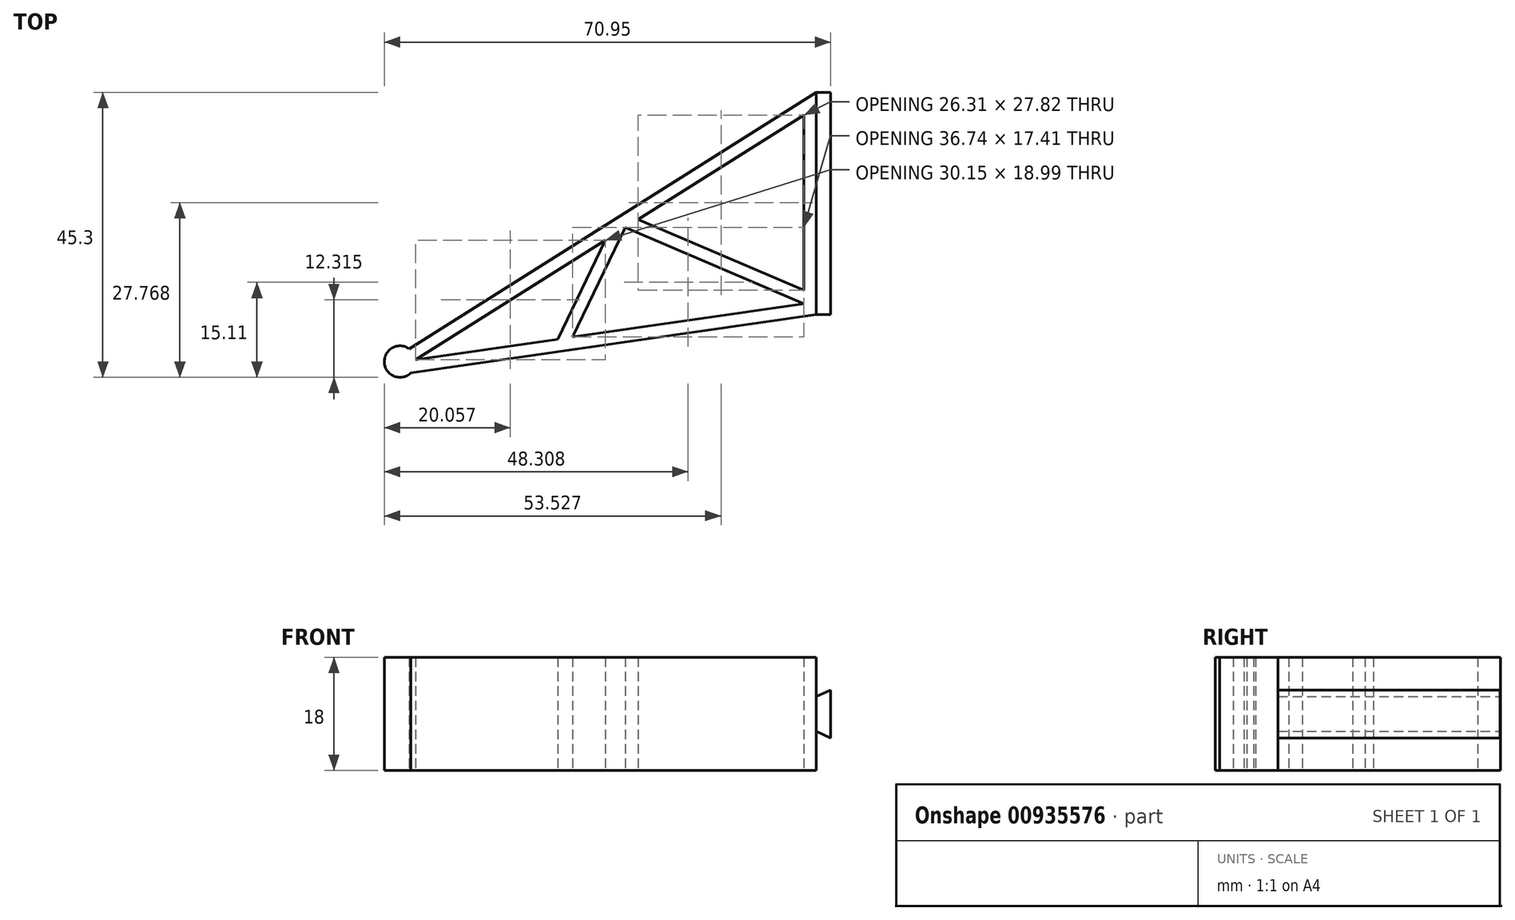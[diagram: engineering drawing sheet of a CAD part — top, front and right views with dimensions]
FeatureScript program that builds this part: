
annotation { "Feature Type Name" : "Feature", "Feature Type Description" : "" }
export const myFeature = defineFeature(function(context is Context, id is Id, definition is map)
    precondition{}
    {
        {
            var Q0;
            Q0=qCreatedBy(makeId("Top.planeOp"),FACE);
            var sketch = newSketch(context, id + "F0", { "sketchPlane" : qUnion([Q0])});
            skLineSegment(sketch, "E0", {"start": v(0, 0) * mm, "end": v(0, 30) * mm});
            skLineSegment(sketch, "E1", {"start": v(0, 30) * mm, "end": v(-61.7, -8.86) * mm});
            skLineSegment(sketch, "E2", {"start": v(-61.7, -8.86) * mm, "end": v(0, 0) * mm});
            skLineSegment(sketch, "E3", {"start": v(0, 0) * mm, "end": v(-28.36, 12.14) * mm});
            skLineSegment(sketch, "E4", {"start": v(-28.36, 12.14) * mm, "end": v(-36.74, -5.28) * mm});
            skLineSegment(sketch, "E5.0", {"start": v(1.45, 1.56) * mm, "end": v(-27.58, 13.97) * mm});
            skLineSegment(sketch, "E6.0", {"start": v(-31.42, 10.4) * mm, "end": v(-40.17, -7.79) * mm});
            skLineSegment(sketch, "E7.0", {"start": v(-0.25, 32.2) * mm, "end": v(-62.73, -7.14) * mm});
            skLineSegment(sketch, "E8.0", {"start": v(-62.45, -10.99) * mm, "end": v(0.28, -1.98) * mm});
            skLineSegment(sketch, "E9.0", {"start": v(2, -1.73) * mm, "end": v(2, 33.62) * mm});
            skCircle(sketch, "E10", {"center": v(-64.18, -9.18) * mm, "radius": 2.5 * mm});
            skLineSegment(sketch, "E11", {"start": v(-0.25, 32.2) * mm, "end": v(0, 30) * mm});
            skLineSegment(sketch, "E12", {"start": v(0, 0) * mm, "end": v(0.28, -1.98) * mm});
            skLineSegment(sketch, "E13", {"start": v(-27.58, 13.97) * mm, "end": v(-28.54, 14.39) * mm});
            skLineSegment(sketch, "E14", {"start": v(-36.74, -5.28) * mm, "end": v(-37.79, -7.45) * mm});
            skLineSegment(sketch, "E15", {"start": v(-31.42, 10.4) * mm, "end": v(-30.45, 13.18) * mm});
            skLineSegment(sketch, "E16", {"start": v(2, 33.62) * mm, "end": v(-0.25, 32.2) * mm});
            skLineSegment(sketch, "E17", {"start": v(0, 30) * mm, "end": v(2, 31.26) * mm});
            skLineSegment(sketch, "E18", {"start": v(2, -1.73) * mm, "end": v(0.28, -1.98) * mm});
            skLineSegment(sketch, "E19", {"start": v(1.45, 1.56) * mm, "end": v(2, 1.32) * mm});
            skSolve(sketch);
        }
        {
            var Q0;
            Q0=makeQuery(id+"F0.imprint","IMPRINT",FACE,{"disambiguationData":[TD([[makeQuery(id+"F0.imprint","IMPRINT",EDGE,{"derivedFrom":sQuery(id+"F0.wireOp",EDGE,"E11")}),1.0]])]});
            var Q1;
            {var subQ0=sQuery(id+"F0.wireOp",EDGE,"E11");Q1=makeQuery(id+"F0.imprint","IMPRINT",FACE,{"disambiguationData":[TD([[makeQuery(id+"F0.imprint","IMPRINT",EDGE,{"derivedFrom":subQ0}),-1.0]])]});}
            var Q2;
            {var subQ0=sQuery(id+"F0.wireOp",EDGE,"E17");Q2=makeQuery(id+"F0.imprint","IMPRINT",FACE,{"disambiguationData":[TD([[makeQuery(id+"F0.imprint","IMPRINT",EDGE,{"derivedFrom":subQ0}),-1.0]])]});}
            var Q3;
            {var subQ6=sQuery(id+"F0.wireOp",EDGE,"E12");Q3=makeQuery(id+"F0.imprint","IMPRINT",FACE,{"disambiguationData":[TD([[makeQuery(id+"F0.imprint","IMPRINT",EDGE,{"derivedFrom":subQ6}),1.0]])]});}
            var Q4;
            {var subQ0=sQuery(id+"F0.wireOp",EDGE,"E12");Q4=makeQuery(id+"F0.imprint","IMPRINT",FACE,{"disambiguationData":[TD([[makeQuery(id+"F0.imprint","IMPRINT",EDGE,{"derivedFrom":subQ0}),-1.0]])]});}
            var Q5;
            {var subQ0=sQuery(id+"F0.wireOp",EDGE,"E3");Q5=makeQuery(id+"F0.imprint","IMPRINT",FACE,{"disambiguationData":[TD([[makeQuery(id+"F0.imprint","IMPRINT",EDGE,{"derivedFrom":subQ0}),-1.0]])]});}
            var Q6;
            {var subQ7=sQuery(id+"F0.wireOp",EDGE,"E13");Q6=makeQuery(id+"F0.imprint","IMPRINT",FACE,{"disambiguationData":[TD([[makeQuery(id+"F0.imprint","IMPRINT",EDGE,{"derivedFrom":subQ7}),1.0]])]});}
            var Q7;
            {var subQ0=sQuery(id+"F0.wireOp",EDGE,"E4");Q7=makeQuery(id+"F0.imprint","IMPRINT",FACE,{"disambiguationData":[TD([[makeQuery(id+"F0.imprint","IMPRINT",EDGE,{"derivedFrom":subQ0}),-1.0]])]});}
            var Q8;
            {var subQ5=sQuery(id+"F0.wireOp",EDGE,"E15");Q8=makeQuery(id+"F0.imprint","IMPRINT",FACE,{"disambiguationData":[TD([[makeQuery(id+"F0.imprint","IMPRINT",EDGE,{"derivedFrom":subQ5}),1.0]])]});}
            var Q9;
            {var subQ3=sQuery(id+"F0.wireOp",EDGE,"E6.0");var subQ5=sQuery(id+"F0.wireOp",EDGE,"E8.0");var subQ6=makeQuery(id+"F0.imprint","INTERSECT",VERTEX,{"derivedFrom":[subQ3,subQ5]});Q9=makeQuery(id+"F0.imprint","IMPRINT",FACE,{"disambiguationData":[TD([[makeQuery(id+"F0.imprint","IMPRINT",EDGE,{"disambiguationData":[TD([[subQ6,1.0]])],"derivedFrom":subQ3}),-1.0]])]});}
            var Q10;
            {var subQ0=sQuery(id+"F0.wireOp",EDGE,"E14");Q10=makeQuery(id+"F0.imprint","IMPRINT",FACE,{"disambiguationData":[TD([[makeQuery(id+"F0.imprint","IMPRINT",EDGE,{"derivedFrom":subQ0}),-1.0]])]});}
            var Q11;
            {var subQ0=sQuery(id+"F0.wireOp",EDGE,"E10");var subQ2=makeQuery(id+"F0.imprint","INTERSECT",VERTEX,{"derivedFrom":[sQuery(id+"F0.wireOp",EDGE,"E7.0"),subQ0]});Q11=makeQuery(id+"F0.imprint","IMPRINT",FACE,{"disambiguationData":[TD([[makeQuery(id+"F0.imprint","IMPRINT",EDGE,{"disambiguationData":[TD([[subQ2,-1.0]])],"derivedFrom":subQ0}),1.0]])]});}
            extrude(context, id + "F1", {"entities" : qUnion([Q0, Q1, Q2, Q3, Q4, Q5, Q6, Q7, Q8, Q9, Q10, Q11]), "depth" : 18 * mm, "offsetDistance" : 25 * mm});
        }
        {
            var Q0;
            Q0=qCreatedBy(makeId("Front.planeOp"),FACE);
            var sketch = newSketch(context, id + "F2", { "sketchPlane" : qUnion([Q0])});
            skLineSegment(sketch, "E20", {"start": v(2, 11.75) * mm, "end": v(2, 6.25) * mm});
            skLineSegment(sketch, "E21", {"start": v(2, 11.75) * mm, "end": v(4.27, 12.8) * mm});
            skLineSegment(sketch, "E22", {"start": v(4.27, 12.8) * mm, "end": v(4.27, 5.2) * mm});
            skLineSegment(sketch, "E23", {"start": v(4.27, 5.2) * mm, "end": v(2, 6.25) * mm});
            skSolve(sketch);
        }
        {
            var Q0;
            Q0=makeQuery(id+"F2.imprint","IMPRINT",FACE,{"disambiguationData":[TD([[makeQuery(id+"F2.imprint","IMPRINT",EDGE,{"derivedFrom":sQuery(id+"F2.wireOp",EDGE,"E20")}),1.0]])]});
            extrude(context, id + "F3", {"entities" : qUnion([Q0]), "operationType" : NewBodyOperationType.ADD, "depth" : 1.7 * mm, "offsetDistance" : 25 * mm, "hasSecondDirection" : true, "secondDirectionOppositeDirection" : true, "secondDirectionDepth" : 33.6 * mm});
        }
    });
